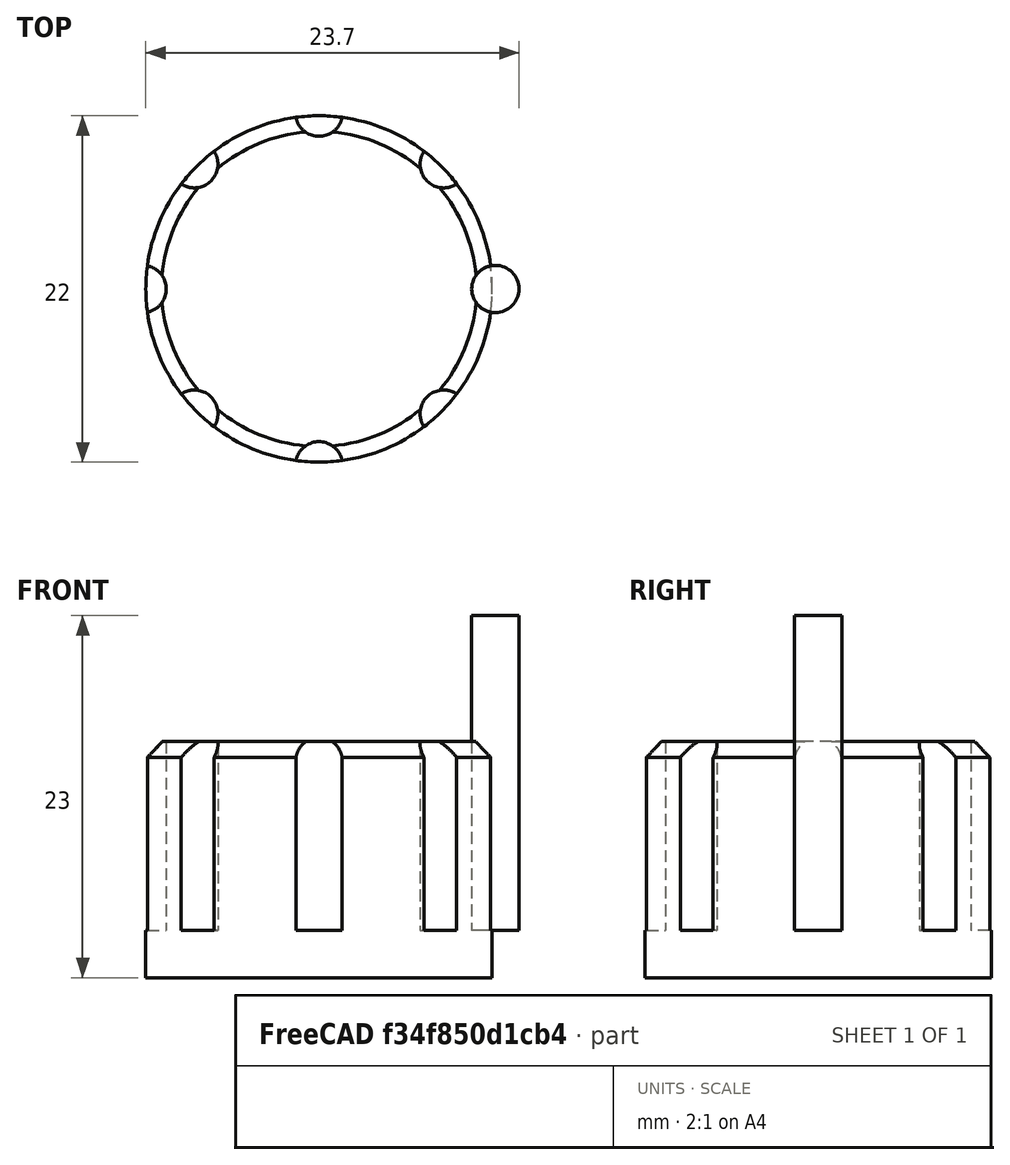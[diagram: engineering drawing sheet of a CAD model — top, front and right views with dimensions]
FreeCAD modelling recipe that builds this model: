
FCSTD DOCUMENT  (FreeCAD 1.0R39319 (Git))
Label: ojt1_t12r01_buttom_potenciometer
License: All rights reserved
LicenseURL: https://en.wikipedia.org/wiki/All_rights_reserved
objects: Part::Chamfer×8, Part::Cylinder×2, Part::FeaturePython×1, Part::Cut×1
note: 11 computed .brp shape members not serialized (recipe doc carries the construction recipe); baked Part::Feature solids carry a one-line shape summary decoded from their .brp

FEATURE [Part::Cylinder] Cylinder  label="base"
  Angle = 360
  AttacherType = Attacher::AttachEngine3D
  FirstAngle = 0
  Height = 15
  Radius = 11
  SecondAngle = 0
FEATURE [Part::Cylinder] Cylinder001  label="Cilindre"
  Angle = 360
  AttacherType = Attacher::AttachEngine3D
  FirstAngle = 0
  Height = 20
  Placement = pos=(11.2,0,3) rot=(0,0,1;0rad)
  Radius = 1.5
  SecondAngle = 0
FEATURE [Part::FeaturePython] Array  # Draft array (typed FeaturePython)
  AlwaysSyncPlacement = false
  Angle = 360
  ArrayType = 1
  Axis = (0,0,1)
  Base = -> Cylinder001
  Center = (0,0,0)
  Count = 8
  ExpandArray = false
  Fuse = false
  IntervalAxis = (0,0,0)
  IntervalX = (100,0,0)
  IntervalY = (0,100,0)
  IntervalZ = (0,0,100)
  NumberCircles = 3
  NumberPolar = 8
  NumberX = 2
  NumberY = 2
  NumberZ = 1
  PlacementList = 8 placements: [(11.2,0,3),(7.9196,7.9196,3),(0,11.2,3),(-7.9196,7.9196,3),(-11.2,1.3716e-15,3),(-7.9196,-7.9196,3),(-2.4869e-15,-11.2,3),(7.9196,-7.9196,3)]
  RadialDistance = 50
  ScaleList = (8) [(1,1,1),(1,1,1),(1,1,1),(1,1,1),(1,1,1),(1,1,1),(1,1,1),(1,1,1)]
  Symmetry = 1
  TangentialDistance = 25
FEATURE [Part::Cut] Cut
  Base = -> Cylinder
  Tool = -> Array
FEATURE [Part::Chamfer] Chamfer
  Base = -> Cut
  EdgeLinks = -> Cut [Edge9]
  Edges = 1 edges r=1: [Edge9]
FEATURE [Part::Chamfer] Chamfer001
  Base = -> Chamfer
  EdgeLinks = -> Chamfer [Edge7]
  Edges = 1 edges r=1: [Edge7]
FEATURE [Part::Chamfer] Chamfer002
  Base = -> Chamfer001
  EdgeLinks = -> Chamfer001 [Edge17]
  Edges = 1 edges r=1: [Edge17]
FEATURE [Part::Chamfer] Chamfer003
  Base = -> Chamfer002
  EdgeLinks = -> Chamfer002 [Edge9]
  Edges = 1 edges r=1: [Edge9]
FEATURE [Part::Chamfer] Chamfer004
  Base = -> Chamfer003
  EdgeLinks = -> Chamfer003 [Edge10]
  Edges = 1 edges r=1: [Edge10]
FEATURE [Part::Chamfer] Chamfer005
  Base = -> Chamfer004
  EdgeLinks = -> Chamfer004 [Edge10]
  Edges = 1 edges r=1: [Edge10]
FEATURE [Part::Chamfer] Chamfer006
  Base = -> Chamfer005
  EdgeLinks = -> Chamfer005 [Edge10]
  Edges = 1 edges r=1: [Edge10]
FEATURE [Part::Chamfer] Chamfer007
  Base = -> Chamfer006
  EdgeLinks = -> Chamfer006 [Edge10]
  Edges = 1 edges r=1: [Edge10]
